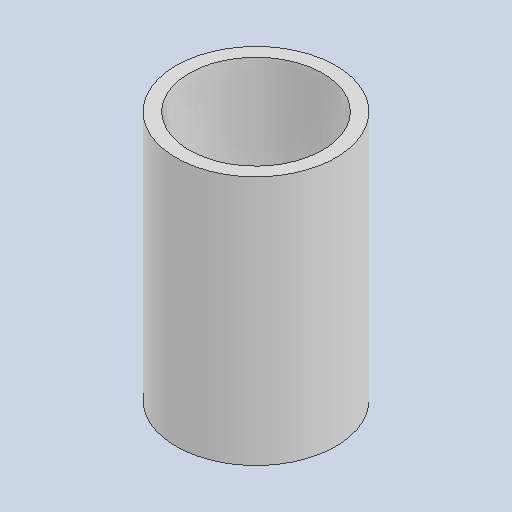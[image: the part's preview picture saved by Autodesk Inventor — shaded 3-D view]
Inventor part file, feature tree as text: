
AUTODESK INVENTOR PART (.ipt)
format: ipt  version: 2025.2 (Build 292293000, 293)  size: 87,552 bytes
history: native  units: in
note: dims shown in document units (in); Inventor stores cm internally (conversion verified against a paired STEP export)
features: other x3, sketch x1
ambient origin geometry x8: Origin, YZ Plane, XZ Plane, XY Plane, X Axis, Y Axis, Z Axis, Center Point
bodies: Solid1 (feature_tree)
feature tree (4):
  other  "Thin_spacer_custom.ipt"
  other  "Solid1::Thin_spacer_custom.ipt"
  other  "TaggingFeature1"
  sketch  "Sketch1"  dims[d0=0.3937in]
